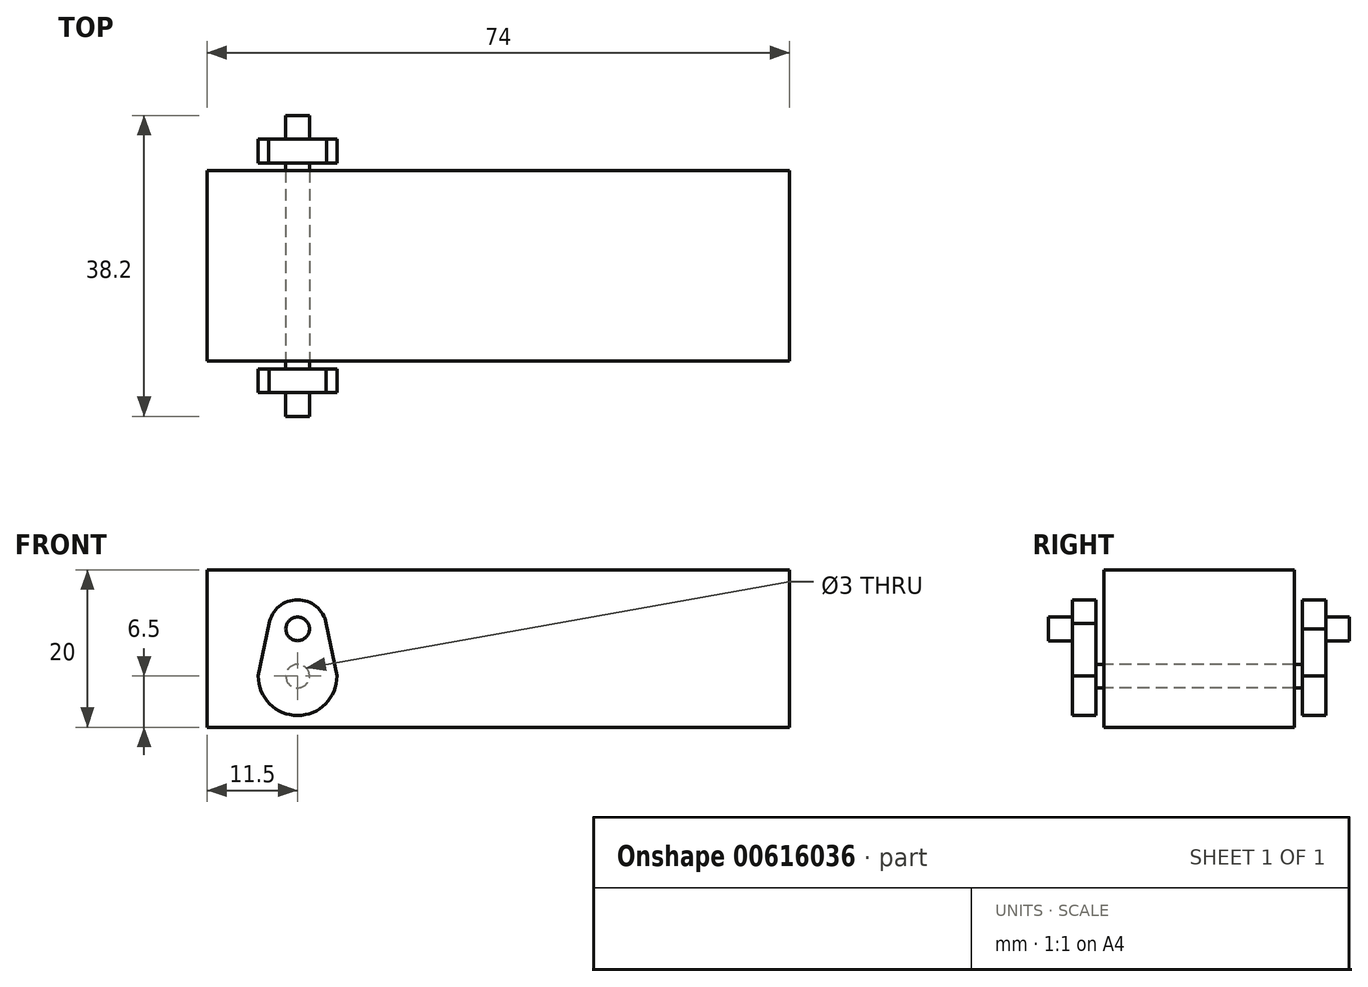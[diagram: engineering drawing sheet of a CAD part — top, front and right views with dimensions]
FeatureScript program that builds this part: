
annotation { "Feature Type Name" : "Feature", "Feature Type Description" : "" }
export const myFeature = defineFeature(function(context is Context, id is Id, definition is map)
    precondition{}
    {
        {
            var Q0;
            Q0=qCreatedBy(makeId("Front.planeOp"),FACE);
            var sketch = newSketch(context, id + "F0", { "sketchPlane" : qUnion([Q0])});
            skLineSegment(sketch, "E0.bottom", {"start": v(37, 0) * mm, "end": v(-37, 0) * mm});
            skLineSegment(sketch, "E0.top", {"start": v(37, 20) * mm, "end": v(-37, 20) * mm});
            skLineSegment(sketch, "E0.left", {"start": v(37, 0) * mm, "end": v(37, 20) * mm});
            skLineSegment(sketch, "E0.right", {"start": v(-37, 0) * mm, "end": v(-37, 20) * mm});
            skPoint(sketch, "E0.middle", {"position": v(0, 10) * mm});
            skCircle(sketch, "E1", {"center": v(-25.5, 6.5) * mm, "radius": 1.5 * mm});
            skSolve(sketch);
        }
        {
            var Q0;
            Q0=makeQuery(id+"F0.imprint","IMPRINT",FACE,{"disambiguationData":[TD([[makeQuery(id+"F0.imprint","IMPRINT",EDGE,{"derivedFrom":sQuery(id+"F0.wireOp",EDGE,"E0.bottom")}),-1.0]])]});
            extrude(context, id + "F1", {"entities" : qUnion([Q0]), "depth" : 12.1 * mm, "offsetDistance" : 25 * mm, "hasSecondDirection" : true, "secondDirectionOppositeDirection" : true, "secondDirectionDepth" : 12.1 * mm});
        }
        {
            var Q0;
            Q0=qCreatedBy(makeId("Front.planeOp"),FACE);
            var sketch = newSketch(context, id + "F2", { "sketchPlane" : qUnion([Q0])});
            skCircle(sketch, "E2", {"center": v(-25.5, 6.5) * mm, "radius": 1.5 * mm});
            skSolve(sketch);
        }
        {
            var Q0;
            Q0 = qSketchRegion(id + "F2", true);
            extrude(context, id + "F3", {"entities" : qUnion([Q0]), "depth" : -16.1 * mm, "offsetDistance" : 25 * mm, "hasSecondDirection" : true, "secondDirectionOppositeDirection" : false, "secondDirectionDepth" : 16.1 * mm});
        }
        {
            var Q0;
            Q0=makeQuery(id+"F3.opExtrude","CAP_FACE",FACE,{"disambiguationData":[OSD([sQuery(id+"F2.wireOp",EDGE,"E2")])],"isStart":true});
            var sketch = newSketch(context, id + "F4", { "sketchPlane" : qUnion([Q0])});
            skArc(sketch, "E3", {"start": v(-30.5, 6.5) * mm, "mid": v(-25.5, 1.5) * mm, "end": v(-20.5, 6.5) * mm});
            skArc(sketch, "E4", {"start": v(-21.86, 13.18) * mm, "mid": v(-25.5, 16.2) * mm, "end": v(-29.14, 13.18) * mm});
            skLineSegment(sketch, "E5", {"start": v(-21.86, 13.18) * mm, "end": v(-20.5, 6.5) * mm});
            skLineSegment(sketch, "E6", {"start": v(-29.14, 13.18) * mm, "end": v(-30.5, 6.5) * mm});
            skSolve(sketch);
        }
        {
            var Q0;
            Q0 = qSketchRegion(id + "F4", true);
            extrude(context, id + "F5", {"entities" : qUnion([Q0]), "operationType" : NewBodyOperationType.ADD, "depth" : -3 * mm, "offsetDistance" : 3 * mm});
        }
        {
            var Q0;
            Q0=makeQuery(id+"F3.opExtrude","CAP_FACE",FACE,{"disambiguationData":[OSD([sQuery(id+"F2.wireOp",EDGE,"E2")])],"isStart":false});
            var sketch = newSketch(context, id + "F6", { "sketchPlane" : qUnion([Q0])});
            skArc(sketch, "E7", {"start": v(20.5, 6.5) * mm, "mid": v(25.5, 1.5) * mm, "end": v(30.5, 6.5) * mm});
            skArc(sketch, "E8", {"start": v(29.2, 12.5) * mm, "mid": v(25.5, 16.2) * mm, "end": v(21.8, 12.5) * mm});
            skLineSegment(sketch, "E9", {"start": v(29.2, 12.5) * mm, "end": v(30.5, 6.5) * mm});
            skLineSegment(sketch, "E10", {"start": v(21.8, 12.5) * mm, "end": v(20.5, 6.5) * mm});
            skSolve(sketch);
        }
        {
            var Q0;
            Q0 = qSketchRegion(id + "F6", true);
            extrude(context, id + "F7", {"entities" : qUnion([Q0]), "operationType" : NewBodyOperationType.ADD, "depth" : -3 * mm, "offsetDistance" : 25 * mm});
        }
        {
            var Q0;
            Q0=makeQuery(id+"F5.boolean.opBoolean","MERGE",FACE,{"derivedFrom":[makeQuery(id+"F3.opExtrude","CAP_FACE",FACE,{"disambiguationData":[OSD([sQuery(id+"F2.wireOp",EDGE,"E2")])],"isStart":true}),makeQuery(id+"F5.opExtrude","CAP_FACE",FACE,{"disambiguationData":[OSD([sQuery(id+"F4.wireOp",EDGE,"E3"),sQuery(id+"F4.wireOp",EDGE,"E4"),sQuery(id+"F4.wireOp",EDGE,"E5"),sQuery(id+"F4.wireOp",EDGE,"E6")])],"isStart":true})]});
            var sketch = newSketch(context, id + "F8", { "sketchPlane" : qUnion([Q0])});
            skCircle(sketch, "E11", {"center": v(-25.5, 12.5) * mm, "radius": 1.5 * mm});
            skSolve(sketch);
        }
        {
            var Q0;
            Q0 = qSketchRegion(id + "F8", true);
            extrude(context, id + "F9", {"entities" : qUnion([Q0]), "operationType" : NewBodyOperationType.ADD, "depth" : 3 * mm, "offsetDistance" : 25 * mm});
        }
        {
            var Q0;
            Q0=makeQuery(id+"F7.boolean.opBoolean","MERGE",FACE,{"derivedFrom":[makeQuery(id+"F3.opExtrude","CAP_FACE",FACE,{"disambiguationData":[OSD([sQuery(id+"F2.wireOp",EDGE,"E2")])],"isStart":false}),makeQuery(id+"F7.opExtrude","CAP_FACE",FACE,{"disambiguationData":[OSD([sQuery(id+"F6.wireOp",EDGE,"E7"),sQuery(id+"F6.wireOp",EDGE,"E8"),sQuery(id+"F6.wireOp",EDGE,"E9"),sQuery(id+"F6.wireOp",EDGE,"E10")])],"isStart":true})]});
            var sketch = newSketch(context, id + "F10", { "sketchPlane" : qUnion([Q0])});
            skCircle(sketch, "E12", {"center": v(25.5, 12.5) * mm, "radius": 1.5 * mm});
            skSolve(sketch);
        }
        {
            var Q0;
            Q0 = qSketchRegion(id + "F10", true);
            extrude(context, id + "F11", {"entities" : qUnion([Q0]), "operationType" : NewBodyOperationType.ADD, "depth" : 3 * mm, "offsetDistance" : 25 * mm});
        }
    });
